# Revit family: QF_ELECTROLUX PROFESSIONAL_CC0FW2_CC0FW2
name_source: partatom
category: Attrezzature speciali
units: mm (PartAtom-declared; Revit-internal decimal feet)

## family parameters
Basato su piano di lavoro = No
Condiviso = No
Punto di calcolo locali = No
Quota connettore circolare = Usa diametro
Sempre verticale = Sì
Taglio con vuoti quando caricato = No
Tipo di parte = Normale

## types (1)
- QF_ELECTROLUX PROFESSIONAL_CC0FW2_CC0FW2
    Accessory = Sì
    Depth Actual = 920 mm  [stored 3.01837 ft]
    Descrizione = STEAM ELEC.POT&PAN WASH+D.PUMP+DET1550MM
    Height Actual = 1785 mm  [stored 5.8563 ft]
    Item Number = 506057
    Length Actual = 2080 mm  [stored 6.82415 ft]
    Modello = ZPPWSLG
    Produttore = Zanussi
    Prospetto di default = 0 mm  [stored 0 ft]
    URL = http://professional.electrolux.com
    URL Manufacturer = http://professional.electrolux.com
    Weight = 0.00 kg

note: [stored X ft] marks values corroborated as IEEE doubles in the binary element streams (Revit-internal decimal feet)

## geometry (parser evidence)
native form markers: Blend x2, Sweep x3
no freeform markers — native parametric forms only
